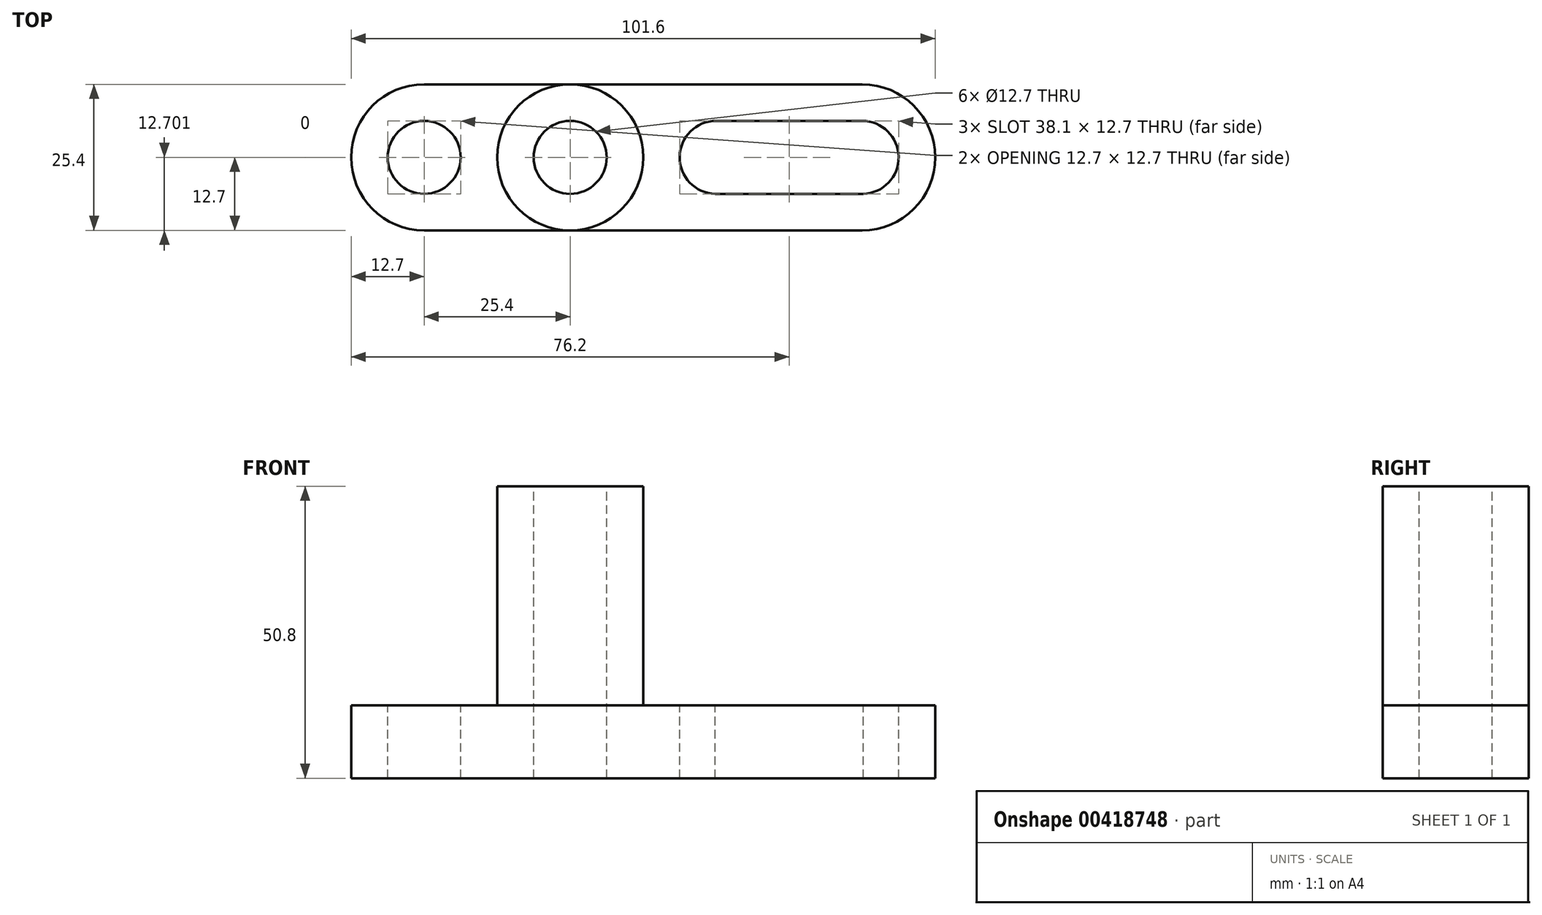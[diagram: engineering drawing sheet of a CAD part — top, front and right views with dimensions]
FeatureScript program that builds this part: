
annotation { "Feature Type Name" : "Feature", "Feature Type Description" : "" }
export const myFeature = defineFeature(function(context is Context, id is Id, definition is map)
    precondition{}
    {
        {
            var Q0;
            Q0=qCreatedBy(makeId("Front.planeOp"),FACE);
            var sketch = newSketch(context, id + "F0", { "sketchPlane" : qUnion([Q0])});
            skLineSegment(sketch, "E0", {"start": v(0, 0) * mm, "end": v(-101.6, 0) * mm});
            skLineSegment(sketch, "E1", {"start": v(-101.6, 0) * mm, "end": v(-101.6, 12.7) * mm});
            skLineSegment(sketch, "E2", {"start": v(-101.6, 12.7) * mm, "end": v(-76.2, 12.7) * mm});
            skLineSegment(sketch, "E3", {"start": v(-76.2, 12.7) * mm, "end": v(-76.2, 50.8) * mm});
            skLineSegment(sketch, "E4", {"start": v(-76.2, 50.8) * mm, "end": v(-50.8, 50.8) * mm});
            skLineSegment(sketch, "E5", {"start": v(-50.8, 50.8) * mm, "end": v(-50.8, 12.7) * mm});
            skLineSegment(sketch, "E6", {"start": v(-50.8, 12.7) * mm, "end": v(0, 12.7) * mm});
            skLineSegment(sketch, "E7", {"start": v(0, 12.7) * mm, "end": v(0, 0) * mm});
            skSolve(sketch);
        }
        {
            var Q0;
            Q0=makeQuery(id+"F0.imprint","IMPRINT",FACE,{"disambiguationData":[TD([[makeQuery(id+"F0.imprint","IMPRINT",EDGE,{"derivedFrom":sQuery(id+"F0.wireOp",EDGE,"E0")}),-1.0]])]});
            extrude(context, id + "F1", {"entities" : qUnion([Q0]), "depth" : 25.4 * mm});
        }
        {
            var Q0;
            Q0=makeQuery(id+"F1.opExtrude","SWEPT_FACE",FACE,{"disambiguationData":[OSD([sQuery(id+"F0.wireOp",EDGE,"E4")])]});
            var sketch = newSketch(context, id + "F2", { "sketchPlane" : qUnion([Q0])});
            skCircle(sketch, "E8", {"center": v(-63.5, -12.7) * mm, "radius": 12.7 * mm});
            skSolve(sketch);
        }
        {
            var Q0;
            {var subQ0=sQuery(id+"F2.wireOp",EDGE,"E8");var subQ1=sQuery(id+"F0.wireOp",EDGE,"E4");var subQ2=makeQuery(id+"F1.opExtrude","CAP_EDGE",EDGE,{"disambiguationData":[OSD([subQ1])],"isStart":true});var subQ3=makeQuery(id+"F2.imprint","INTERSECT",VERTEX,{"derivedFrom":[subQ2,subQ0]});Q0=makeQuery(id+"F2.imprint","IMPRINT",FACE,{"disambiguationData":[TD([[makeQuery(id+"F2.imprint","IMPRINT",EDGE,{"disambiguationData":[TD([[subQ3,1.0]])],"derivedFrom":subQ0}),-1.0]])]});}
            var Q1;
            {var subQ0=sQuery(id+"F2.wireOp",EDGE,"E8");var subQ1=sQuery(id+"F0.wireOp",EDGE,"E4");var subQ2=makeQuery(id+"F1.opExtrude","CAP_EDGE",EDGE,{"disambiguationData":[OSD([subQ1])],"isStart":true});var subQ3=makeQuery(id+"F2.imprint","INTERSECT",VERTEX,{"derivedFrom":[subQ2,subQ0]});Q1=makeQuery(id+"F2.imprint","IMPRINT",FACE,{"disambiguationData":[TD([[makeQuery(id+"F2.imprint","IMPRINT",EDGE,{"disambiguationData":[TD([[subQ3,-1.0]])],"derivedFrom":subQ0}),-1.0]])]});}
            var Q2;
            {var subQ0=sQuery(id+"F2.wireOp",EDGE,"E8");var subQ1=sQuery(id+"F0.wireOp",EDGE,"E4");var subQ4=makeQuery(id+"F1.opExtrude","CAP_EDGE",EDGE,{"disambiguationData":[OSD([subQ1])],"isStart":false});var subQ5=makeQuery(id+"F2.imprint","INTERSECT",VERTEX,{"derivedFrom":[subQ4,subQ0]});Q2=makeQuery(id+"F2.imprint","IMPRINT",FACE,{"disambiguationData":[TD([[makeQuery(id+"F2.imprint","IMPRINT",EDGE,{"disambiguationData":[TD([[subQ5,1.0]])],"derivedFrom":subQ0}),-1.0]])]});}
            var Q3;
            {var subQ0=sQuery(id+"F2.wireOp",EDGE,"E8");var subQ1=sQuery(id+"F0.wireOp",EDGE,"E4");var subQ4=makeQuery(id+"F1.opExtrude","CAP_EDGE",EDGE,{"disambiguationData":[OSD([subQ1])],"isStart":false});var subQ5=makeQuery(id+"F2.imprint","INTERSECT",VERTEX,{"derivedFrom":[subQ4,subQ0]});Q3=makeQuery(id+"F2.imprint","IMPRINT",FACE,{"disambiguationData":[TD([[makeQuery(id+"F2.imprint","IMPRINT",EDGE,{"disambiguationData":[TD([[subQ5,-1.0]])],"derivedFrom":subQ0}),-1.0]])]});}
            extrude(context, id + "F3", {"entities" : qUnion([Q0, Q1, Q2, Q3]), "operationType" : NewBodyOperationType.REMOVE, "oppositeDirection" : true, "depth" : 38.1 * mm});
        }
        {
            var Q0;
            Q0=makeQuery(id+"F1.opExtrude","SWEPT_FACE",FACE,{"disambiguationData":[OSD([sQuery(id+"F0.wireOp",EDGE,"E4")])]});
            var sketch = newSketch(context, id + "F4", { "sketchPlane" : qUnion([Q0])});
            skCircle(sketch, "E9", {"center": v(-63.5, -12.7) * mm, "radius": 6.35 * mm});
            skSolve(sketch);
        }
        {
            var Q0;
            Q0=makeQuery(id+"F4.imprint","IMPRINT",FACE,{"disambiguationData":[TD([[makeQuery(id+"F4.imprint","IMPRINT",EDGE,{"derivedFrom":sQuery(id+"F4.wireOp",EDGE,"E9")}),1.0]])]});
            extrude(context, id + "F5", {"entities" : qUnion([Q0]), "operationType" : NewBodyOperationType.REMOVE, "oppositeDirection" : true, "depth" : 63.5 * mm});
        }
        {
            var Q0;
            {var subQ0=sQuery(id+"F0.wireOp",EDGE,"E4");var subQ1=makeQuery(id+"F1.opExtrude","CAP_EDGE",EDGE,{"disambiguationData":[OSD([subQ0])],"isStart":false});var subQ2=sQuery(id+"F0.wireOp",EDGE,"E3");var subQ3=makeQuery(id+"F1.opExtrude","SWEPT_EDGE",EDGE,{"disambiguationData":[OSD([subQ2,subQ0])]});var subQ4=makeQuery(id+"F2.imprint","INTERSECT",VERTEX,{"derivedFrom":[subQ3,subQ1]});var subQ5=sQuery(id+"F2.wireOp",EDGE,"E8");var subQ6=makeQuery(id+"F2.imprint","INTERSECT",VERTEX,{"derivedFrom":[subQ1,subQ5]});var subQ8=makeQuery(id+"F1.opExtrude","CAP_EDGE",EDGE,{"disambiguationData":[OSD([subQ0])],"isStart":true});var subQ9=makeQuery(id+"F2.imprint","INTERSECT",VERTEX,{"derivedFrom":[subQ3,subQ8]});var subQ10=makeQuery(id+"F2.imprint","INTERSECT",VERTEX,{"derivedFrom":[subQ8,subQ5]});Q0=makeQuery(id+"F3.boolean.opBoolean","MERGE",FACE,{"derivedFrom":[makeQuery(id+"F1.opExtrude","SWEPT_FACE",FACE,{"disambiguationData":[OSD([sQuery(id+"F0.wireOp",EDGE,"E2")])]}),makeQuery(id+"F3.opExtrude","CAP_FACE",FACE,{"disambiguationData":[OSD([subQ2,subQ0,subQ5]),TDD([makeQuery(id+"F2.imprint","IMPRINT",EDGE,{"disambiguationData":[TD([[subQ10,-1.0]])],"derivedFrom":subQ5}),makeQuery(id+"F2.imprint","IMPRINT",EDGE,{"disambiguationData":[TD([[subQ9,1.0]])],"derivedFrom":subQ3}),makeQuery(id+"F2.imprint","IMPRINT",EDGE,{"disambiguationData":[TD([[subQ10,1.0]])],"derivedFrom":subQ8})])],"isStart":false}),makeQuery(id+"F3.opExtrude","CAP_FACE",FACE,{"disambiguationData":[OSD([subQ2,subQ0,subQ5]),TDD([makeQuery(id+"F2.imprint","IMPRINT",EDGE,{"disambiguationData":[TD([[subQ6,1.0]])],"derivedFrom":subQ5}),makeQuery(id+"F2.imprint","IMPRINT",EDGE,{"disambiguationData":[TD([[subQ4,-1.0]])],"derivedFrom":subQ3}),makeQuery(id+"F2.imprint","IMPRINT",EDGE,{"disambiguationData":[TD([[subQ6,1.0]])],"derivedFrom":subQ1})])],"isStart":false})]});}
            var sketch = newSketch(context, id + "F6", { "sketchPlane" : qUnion([Q0])});
            skCircle(sketch, "E10", {"center": v(-88.9, -12.7) * mm, "radius": 6.35 * mm});
            skSolve(sketch);
        }
        {
            var Q0;
            Q0=makeQuery(id+"F6.imprint","IMPRINT",FACE,{"disambiguationData":[TD([[makeQuery(id+"F6.imprint","IMPRINT",EDGE,{"derivedFrom":sQuery(id+"F6.wireOp",EDGE,"E10")}),1.0]])]});
            extrude(context, id + "F7", {"entities" : qUnion([Q0]), "operationType" : NewBodyOperationType.REMOVE, "oppositeDirection" : true, "depth" : 25.4 * mm});
        }
        {
            var Q0;
            {var subQ0=sQuery(id+"F0.wireOp",EDGE,"E4");var subQ1=makeQuery(id+"F1.opExtrude","CAP_EDGE",EDGE,{"disambiguationData":[OSD([subQ0])],"isStart":false});var subQ2=sQuery(id+"F0.wireOp",EDGE,"E3");var subQ3=makeQuery(id+"F1.opExtrude","SWEPT_EDGE",EDGE,{"disambiguationData":[OSD([subQ2,subQ0])]});var subQ4=makeQuery(id+"F2.imprint","INTERSECT",VERTEX,{"derivedFrom":[subQ3,subQ1]});var subQ5=sQuery(id+"F2.wireOp",EDGE,"E8");var subQ6=makeQuery(id+"F2.imprint","INTERSECT",VERTEX,{"derivedFrom":[subQ1,subQ5]});var subQ8=makeQuery(id+"F1.opExtrude","CAP_EDGE",EDGE,{"disambiguationData":[OSD([subQ0])],"isStart":true});var subQ9=makeQuery(id+"F2.imprint","INTERSECT",VERTEX,{"derivedFrom":[subQ3,subQ8]});var subQ10=makeQuery(id+"F2.imprint","INTERSECT",VERTEX,{"derivedFrom":[subQ8,subQ5]});Q0=makeQuery(id+"F3.boolean.opBoolean","MERGE",FACE,{"derivedFrom":[makeQuery(id+"F1.opExtrude","SWEPT_FACE",FACE,{"disambiguationData":[OSD([sQuery(id+"F0.wireOp",EDGE,"E2")])]}),makeQuery(id+"F3.opExtrude","CAP_FACE",FACE,{"disambiguationData":[OSD([subQ2,subQ0,subQ5]),TDD([makeQuery(id+"F2.imprint","IMPRINT",EDGE,{"disambiguationData":[TD([[subQ10,-1.0]])],"derivedFrom":subQ5}),makeQuery(id+"F2.imprint","IMPRINT",EDGE,{"disambiguationData":[TD([[subQ9,1.0]])],"derivedFrom":subQ3}),makeQuery(id+"F2.imprint","IMPRINT",EDGE,{"disambiguationData":[TD([[subQ10,1.0]])],"derivedFrom":subQ8})])],"isStart":false}),makeQuery(id+"F3.opExtrude","CAP_FACE",FACE,{"disambiguationData":[OSD([subQ2,subQ0,subQ5]),TDD([makeQuery(id+"F2.imprint","IMPRINT",EDGE,{"disambiguationData":[TD([[subQ6,1.0]])],"derivedFrom":subQ5}),makeQuery(id+"F2.imprint","IMPRINT",EDGE,{"disambiguationData":[TD([[subQ4,-1.0]])],"derivedFrom":subQ3}),makeQuery(id+"F2.imprint","IMPRINT",EDGE,{"disambiguationData":[TD([[subQ6,1.0]])],"derivedFrom":subQ1})])],"isStart":false})]});}
            var sketch = newSketch(context, id + "F8", { "sketchPlane" : qUnion([Q0])});
            skCircle(sketch, "E11", {"center": v(-88.9, -12.7) * mm, "radius": 12.7 * mm});
            skSolve(sketch);
        }
        {
            var Q0;
            {var subQ0=sQuery(id+"F8.wireOp",EDGE,"E11");var subQ3=sQuery(id+"F0.wireOp",EDGE,"E2");var subQ6=makeQuery(id+"F1.opExtrude","SWEPT_EDGE",EDGE,{"disambiguationData":[OSD([sQuery(id+"F0.wireOp",EDGE,"E1"),subQ3])]});var subQ7=makeQuery(id+"F8.imprint","INTERSECT",VERTEX,{"derivedFrom":[subQ6,subQ0]});Q0=makeQuery(id+"F8.imprint","IMPRINT",FACE,{"disambiguationData":[TD([[makeQuery(id+"F8.imprint","IMPRINT",EDGE,{"disambiguationData":[TD([[subQ7,1.0]])],"derivedFrom":subQ0}),-1.0]])]});}
            var Q1;
            {var subQ0=sQuery(id+"F8.wireOp",EDGE,"E11");var subQ1=sQuery(id+"F0.wireOp",EDGE,"E2");var subQ2=makeQuery(id+"F1.opExtrude","SWEPT_EDGE",EDGE,{"disambiguationData":[OSD([sQuery(id+"F0.wireOp",EDGE,"E1"),subQ1])]});var subQ3=makeQuery(id+"F8.imprint","INTERSECT",VERTEX,{"derivedFrom":[subQ2,subQ0]});Q1=makeQuery(id+"F8.imprint","IMPRINT",FACE,{"disambiguationData":[TD([[makeQuery(id+"F8.imprint","IMPRINT",EDGE,{"disambiguationData":[TD([[subQ3,-1.0]])],"derivedFrom":subQ0}),-1.0]])]});}
            extrude(context, id + "F9", {"entities" : qUnion([Q0, Q1]), "operationType" : NewBodyOperationType.REMOVE, "oppositeDirection" : true, "depth" : 25.4 * mm});
        }
        {
            var Q0;
            {var subQ0=sQuery(id+"F0.wireOp",EDGE,"E4");var subQ1=makeQuery(id+"F1.opExtrude","CAP_EDGE",EDGE,{"disambiguationData":[OSD([subQ0])],"isStart":false});var subQ2=sQuery(id+"F0.wireOp",EDGE,"E5");var subQ3=makeQuery(id+"F1.opExtrude","SWEPT_EDGE",EDGE,{"disambiguationData":[OSD([subQ0,subQ2])]});var subQ4=makeQuery(id+"F2.imprint","INTERSECT",VERTEX,{"derivedFrom":[subQ3,subQ1]});var subQ5=sQuery(id+"F2.wireOp",EDGE,"E8");var subQ6=makeQuery(id+"F2.imprint","INTERSECT",VERTEX,{"derivedFrom":[subQ1,subQ5]});var subQ8=makeQuery(id+"F1.opExtrude","CAP_EDGE",EDGE,{"disambiguationData":[OSD([subQ0])],"isStart":true});var subQ9=makeQuery(id+"F2.imprint","INTERSECT",VERTEX,{"derivedFrom":[subQ3,subQ8]});var subQ10=makeQuery(id+"F2.imprint","INTERSECT",VERTEX,{"derivedFrom":[subQ8,subQ5]});Q0=makeQuery(id+"F3.boolean.opBoolean","MERGE",FACE,{"derivedFrom":[makeQuery(id+"F1.opExtrude","SWEPT_FACE",FACE,{"disambiguationData":[OSD([sQuery(id+"F0.wireOp",EDGE,"E6")])]}),makeQuery(id+"F3.opExtrude","CAP_FACE",FACE,{"disambiguationData":[OSD([subQ0,subQ2,subQ5]),TDD([makeQuery(id+"F2.imprint","IMPRINT",EDGE,{"disambiguationData":[TD([[subQ10,1.0]])],"derivedFrom":subQ5}),makeQuery(id+"F2.imprint","IMPRINT",EDGE,{"disambiguationData":[TD([[subQ9,1.0]])],"derivedFrom":subQ3}),makeQuery(id+"F2.imprint","IMPRINT",EDGE,{"disambiguationData":[TD([[subQ10,-1.0]])],"derivedFrom":subQ8})])],"isStart":false}),makeQuery(id+"F3.opExtrude","CAP_FACE",FACE,{"disambiguationData":[OSD([subQ0,subQ2,subQ5]),TDD([makeQuery(id+"F2.imprint","IMPRINT",EDGE,{"disambiguationData":[TD([[subQ6,-1.0]])],"derivedFrom":subQ5}),makeQuery(id+"F2.imprint","IMPRINT",EDGE,{"disambiguationData":[TD([[subQ4,-1.0]])],"derivedFrom":subQ3}),makeQuery(id+"F2.imprint","IMPRINT",EDGE,{"disambiguationData":[TD([[subQ6,-1.0]])],"derivedFrom":subQ1})])],"isStart":false})]});}
            var sketch = newSketch(context, id + "F10", { "sketchPlane" : qUnion([Q0])});
            skCircle(sketch, "E12", {"center": v(-38.1, -12.7) * mm, "radius": 6.35 * mm});
            skCircle(sketch, "E13", {"center": v(-12.7, -12.7) * mm, "radius": 6.35 * mm});
            skLineSegment(sketch, "E14", {"start": v(-38.1, -6.35) * mm, "end": v(-12.7, -6.35) * mm});
            skLineSegment(sketch, "E15", {"start": v(-38.29, -19.05) * mm, "end": v(-12.51, -19.05) * mm});
            skSolve(sketch);
        }
        {
            var Q0;
            {var subQ0=sQuery(id+"F10.wireOp",EDGE,"E12");var subQ1=makeQuery(id+"F10.imprint","INTERSECT",VERTEX,{"derivedFrom":[subQ0,sQuery(id+"F10.wireOp",EDGE,"E14")]});Q0=makeQuery(id+"F10.imprint","IMPRINT",FACE,{"disambiguationData":[TD([[makeQuery(id+"F10.imprint","IMPRINT",EDGE,{"disambiguationData":[TD([[subQ1,-1.0]])],"derivedFrom":subQ0}),1.0]])]});}
            var Q1;
            {var subQ0=sQuery(id+"F10.wireOp",EDGE,"E14");Q1=makeQuery(id+"F10.imprint","IMPRINT",FACE,{"disambiguationData":[TD([[makeQuery(id+"F10.imprint","IMPRINT",EDGE,{"derivedFrom":subQ0}),-1.0]])]});}
            var Q2;
            {var subQ0=sQuery(id+"F10.wireOp",EDGE,"E13");var subQ1=makeQuery(id+"F10.imprint","INTERSECT",VERTEX,{"derivedFrom":[subQ0,sQuery(id+"F10.wireOp",EDGE,"E14")]});Q2=makeQuery(id+"F10.imprint","IMPRINT",FACE,{"disambiguationData":[TD([[makeQuery(id+"F10.imprint","IMPRINT",EDGE,{"disambiguationData":[TD([[subQ1,-1.0]])],"derivedFrom":subQ0}),1.0]])]});}
            extrude(context, id + "F11", {"entities" : qUnion([Q0, Q1, Q2]), "operationType" : NewBodyOperationType.REMOVE, "oppositeDirection" : true, "depth" : 25.4 * mm});
        }
        {
            var Q0;
            {var subQ0=sQuery(id+"F0.wireOp",EDGE,"E4");var subQ1=makeQuery(id+"F1.opExtrude","CAP_EDGE",EDGE,{"disambiguationData":[OSD([subQ0])],"isStart":false});var subQ2=sQuery(id+"F0.wireOp",EDGE,"E5");var subQ3=makeQuery(id+"F1.opExtrude","SWEPT_EDGE",EDGE,{"disambiguationData":[OSD([subQ0,subQ2])]});var subQ4=makeQuery(id+"F2.imprint","INTERSECT",VERTEX,{"derivedFrom":[subQ3,subQ1]});var subQ5=sQuery(id+"F2.wireOp",EDGE,"E8");var subQ6=makeQuery(id+"F2.imprint","INTERSECT",VERTEX,{"derivedFrom":[subQ1,subQ5]});var subQ8=makeQuery(id+"F1.opExtrude","CAP_EDGE",EDGE,{"disambiguationData":[OSD([subQ0])],"isStart":true});var subQ9=makeQuery(id+"F2.imprint","INTERSECT",VERTEX,{"derivedFrom":[subQ3,subQ8]});var subQ10=makeQuery(id+"F2.imprint","INTERSECT",VERTEX,{"derivedFrom":[subQ8,subQ5]});Q0=makeQuery(id+"F3.boolean.opBoolean","MERGE",FACE,{"derivedFrom":[makeQuery(id+"F1.opExtrude","SWEPT_FACE",FACE,{"disambiguationData":[OSD([sQuery(id+"F0.wireOp",EDGE,"E6")])]}),makeQuery(id+"F3.opExtrude","CAP_FACE",FACE,{"disambiguationData":[OSD([subQ0,subQ2,subQ5]),TDD([makeQuery(id+"F2.imprint","IMPRINT",EDGE,{"disambiguationData":[TD([[subQ10,1.0]])],"derivedFrom":subQ5}),makeQuery(id+"F2.imprint","IMPRINT",EDGE,{"disambiguationData":[TD([[subQ9,1.0]])],"derivedFrom":subQ3}),makeQuery(id+"F2.imprint","IMPRINT",EDGE,{"disambiguationData":[TD([[subQ10,-1.0]])],"derivedFrom":subQ8})])],"isStart":false}),makeQuery(id+"F3.opExtrude","CAP_FACE",FACE,{"disambiguationData":[OSD([subQ0,subQ2,subQ5]),TDD([makeQuery(id+"F2.imprint","IMPRINT",EDGE,{"disambiguationData":[TD([[subQ6,-1.0]])],"derivedFrom":subQ5}),makeQuery(id+"F2.imprint","IMPRINT",EDGE,{"disambiguationData":[TD([[subQ4,-1.0]])],"derivedFrom":subQ3}),makeQuery(id+"F2.imprint","IMPRINT",EDGE,{"disambiguationData":[TD([[subQ6,-1.0]])],"derivedFrom":subQ1})])],"isStart":false})]});}
            var sketch = newSketch(context, id + "F12", { "sketchPlane" : qUnion([Q0])});
            skCircle(sketch, "E16", {"center": v(-12.7, -12.7) * mm, "radius": 12.7 * mm});
            skSolve(sketch);
        }
        {
            var Q0;
            {var subQ0=sQuery(id+"F12.wireOp",EDGE,"E16");var subQ3=sQuery(id+"F0.wireOp",EDGE,"E6");var subQ6=makeQuery(id+"F1.opExtrude","SWEPT_EDGE",EDGE,{"disambiguationData":[OSD([subQ3,sQuery(id+"F0.wireOp",EDGE,"E7")])]});var subQ7=makeQuery(id+"F12.imprint","INTERSECT",VERTEX,{"derivedFrom":[subQ6,subQ0]});Q0=makeQuery(id+"F12.imprint","IMPRINT",FACE,{"disambiguationData":[TD([[makeQuery(id+"F12.imprint","IMPRINT",EDGE,{"disambiguationData":[TD([[subQ7,-1.0]])],"derivedFrom":subQ0}),-1.0]])]});}
            var Q1;
            {var subQ0=sQuery(id+"F12.wireOp",EDGE,"E16");var subQ1=sQuery(id+"F0.wireOp",EDGE,"E6");var subQ2=makeQuery(id+"F1.opExtrude","SWEPT_EDGE",EDGE,{"disambiguationData":[OSD([subQ1,sQuery(id+"F0.wireOp",EDGE,"E7")])]});var subQ3=makeQuery(id+"F12.imprint","INTERSECT",VERTEX,{"derivedFrom":[subQ2,subQ0]});Q1=makeQuery(id+"F12.imprint","IMPRINT",FACE,{"disambiguationData":[TD([[makeQuery(id+"F12.imprint","IMPRINT",EDGE,{"disambiguationData":[TD([[subQ3,1.0]])],"derivedFrom":subQ0}),-1.0]])]});}
            extrude(context, id + "F13", {"entities" : qUnion([Q0, Q1]), "operationType" : NewBodyOperationType.REMOVE, "oppositeDirection" : true, "depth" : 25.4 * mm});
        }
    });
